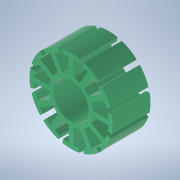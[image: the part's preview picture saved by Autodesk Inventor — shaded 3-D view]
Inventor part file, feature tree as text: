
AUTODESK INVENTOR PART (.ipt)
format: ipt  version: 2022 (Build 260153000, 153)  size: 233,984 bytes
history: native  units: in
note: dims shown in document units (in); Inventor stores cm internally (conversion verified against a paired STEP export)
features: extrude x1, sketch x1
ambient origin geometry x8: Origin, YZ Plane, XZ Plane, XY Plane, X Axis, Y Axis, Z Axis, Center Point
bodies: Solid1 (feature_tree)
feature tree (2):
  extrude  "Extrusion1"  Depth=0.6299in
  sketch  "Sketch1"  dims[d0=1.378in d1=0.5906in d2=0.0689in d3=0.0689in d4=0.0962in d5=0.0394in d6=0.0394in d7=0.0825in d8=4.7244in d10=360.0deg d12=0.6299in d13=0.0in]
